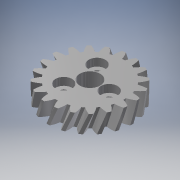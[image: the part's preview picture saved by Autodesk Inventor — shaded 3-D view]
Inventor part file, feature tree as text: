
AUTODESK INVENTOR PART (.ipt)
format: ipt  version: 2017 SP1 (Build 210196100, 196)  size: 842,240 bytes
history: native  units: mm (DEFAULTED — no unit token found)
features: sketch x5, extrude x3, plane x3, other x3, hole x1
ambient origin geometry x8: Origin, YZ Plane, XZ Plane, XY Plane, X Axis, Y Axis, Z Axis, Center Point
bodies: Solid1 (feature_tree)
feature tree (15):
  extrude  "Extrusion1"  Depth=7.0mm TaperAngle=0.0deg
  plane  "Work Plane2"
  plane  "Work Plane8"
  plane  "Work Plane9"
  other  "Engrenage cylindrique"
  extrude  "Extrusion2"  Depth=10.0mm TaperAngle=0.0deg
  hole  "Perçage1"  [1 undecoded]
  extrude  "Extrusion3"  Depth=3.0mm TaperAngle=0.0deg
  sketch  "Sketch1"  dims[d0=32.749068mm d1=7.0mm d2=0.0mm]
  sketch  "Sketch2"  dims[d3=30.066593mm d4=10.0mm d5=0.0mm d16=30.066593mm d17=0.0mm d34=1.570796mm d39=0.0mm d41=0.0mm d43=30.066593mm d46=30.066593mm d47=0.0mm d48=0.0mm d49=8.0mm d50=8.0mm d51=0.0mm d52=15.0mm d53=30.0mm d55=360.0deg d57=3.0mm d58=6.0mm d59=4.0mm d60=2.0mm d61=90.0deg d62=8.0mm d63=20.594885mm d64=6.5mm d65=6.5mm d66=6.5mm d67=3.0mm d68=0.0mm]
  other  "Srf1"
  sketch  "Esquisse3"
  sketch  "Esquisse4"
  sketch  "Esquisse5"
  other  "Diamètre primitif"
note: 1 required parameter value undecoded (feature->parameter linkage not recoverable at this tier; creation-order binding heuristic only, values carry confidence <= 0.55)
